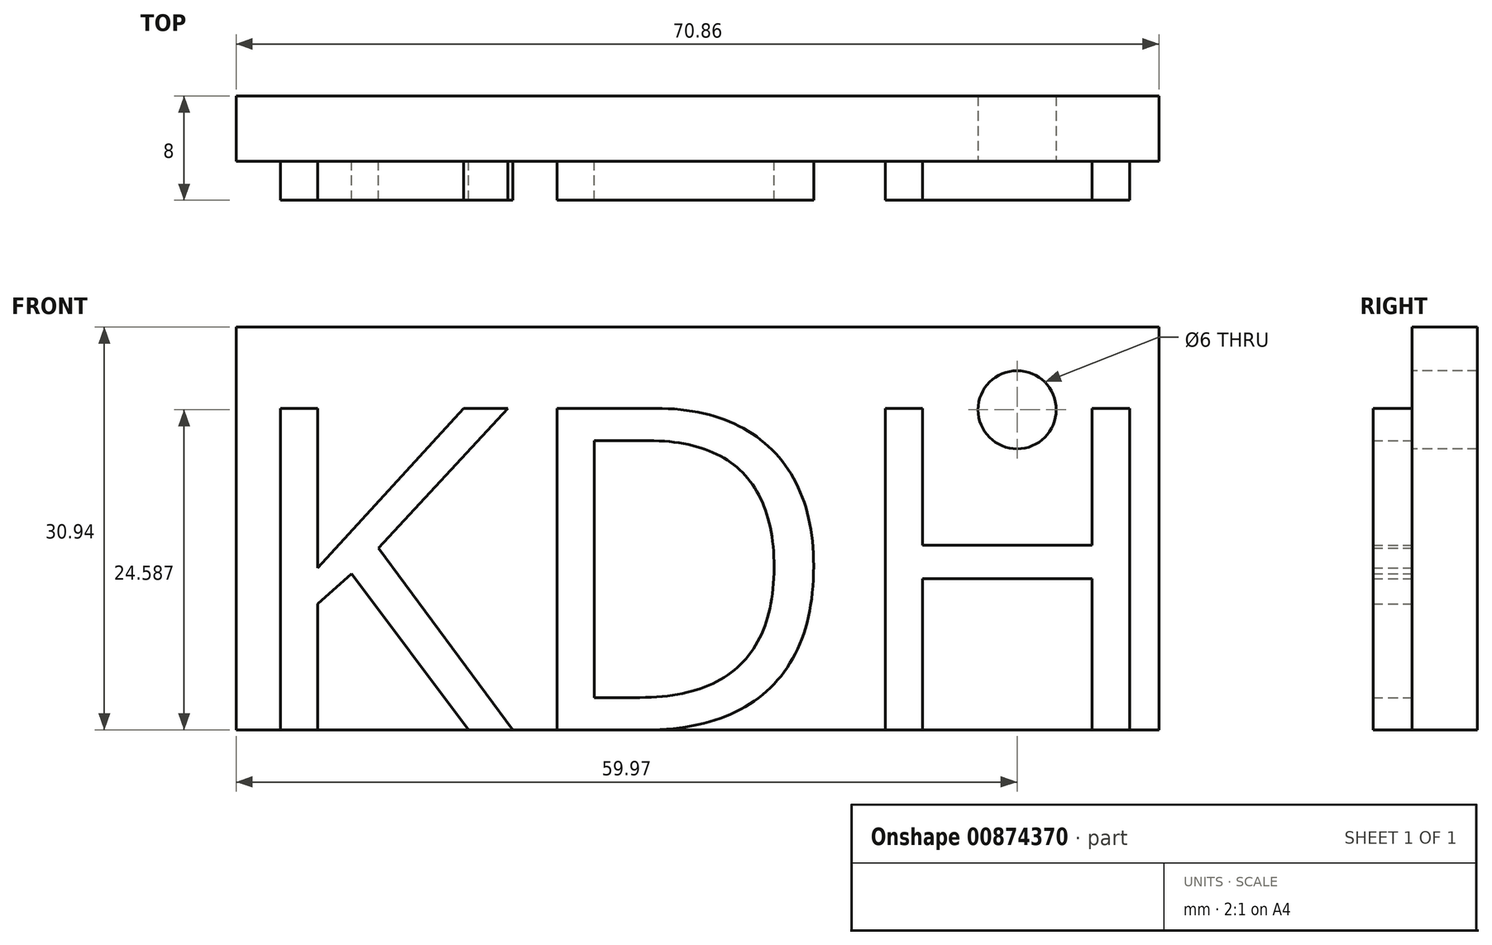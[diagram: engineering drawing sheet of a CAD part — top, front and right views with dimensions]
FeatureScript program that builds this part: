
annotation { "Feature Type Name" : "Feature", "Feature Type Description" : "" }
export const myFeature = defineFeature(function(context is Context, id is Id, definition is map)
    precondition{}
    {
        {
            var Q0;
            Q0=qCreatedBy(makeId("Front.planeOp"),FACE);
            var sketch = newSketch(context, id + "F0", { "sketchPlane" : qUnion([Q0])});
            skLineSegment(sketch, "E0.bottom", {"start": v(0, 0) * mm, "end": v(70.86, 0) * mm});
            skLineSegment(sketch, "E0.top", {"start": v(0, 30.94) * mm, "end": v(70.86, 30.94) * mm});
            skLineSegment(sketch, "E0.left", {"start": v(0, 0) * mm, "end": v(0, 30.94) * mm});
            skLineSegment(sketch, "E0.right", {"start": v(70.86, 0) * mm, "end": v(70.86, 30.94) * mm});
            skSolve(sketch);
        }
        {
            var Q0;
            Q0=makeQuery(id+"F0.imprint","IMPRINT",FACE,{"disambiguationData":[TD([[makeQuery(id+"F0.imprint","IMPRINT",EDGE,{"derivedFrom":sQuery(id+"F0.wireOp",EDGE,"E0.bottom")}),1.0]])]});
            extrude(context, id + "F1", {"entities" : qUnion([Q0]), "depth" : 5 * mm, "offsetDistance" : 25 * mm});
        }
        {
            var Q0;
            Q0=makeQuery(id+"F1.opExtrude","CAP_FACE",FACE,{"disambiguationData":[OSD([sQuery(id+"F0.wireOp",EDGE,"E0.bottom"),sQuery(id+"F0.wireOp",EDGE,"E0.top"),sQuery(id+"F0.wireOp",EDGE,"E0.left"),sQuery(id+"F0.wireOp",EDGE,"E0.right")])],"isStart":false});
            var sketch = newSketch(context, id + "F2", { "sketchPlane" : qUnion([Q0])});
            skText(sketch, "E1", { "text": "KDH", "fontName": "OpenSans-Regular.ttf"});
            const initialGuessF2  = {"E1": [0, 0, 1, 0, 0.02491]};
            skSetInitialGuess(sketch, initialGuessF2);
            skSolve(sketch);
        }
        {
            var Q0;
            Q0 = qSketchRegion(id + "F2", true);
            extrude(context, id + "F3", {"entities" : qUnion([Q0]), "operationType" : NewBodyOperationType.ADD, "depth" : 3 * mm, "offsetDistance" : 25 * mm});
        }
        {
            var Q0;
            {var subQ0=sQuery(id+"F0.wireOp",EDGE,"E0.top");var subQ1=sQuery(id+"F0.wireOp",EDGE,"E0.right");var subQ2=sQuery(id+"F0.wireOp",EDGE,"E0.bottom");var subQ3=sQuery(id+"F0.wireOp",EDGE,"E0.left");Q0=makeQuery(id+"F3.boolean.opBoolean","SPLIT",FACE,{"disambiguationData":[TD([makeQuery(id+"F1.opExtrude","SWEPT_FACE",FACE,{"disambiguationData":[OSD([subQ0])]})])],"derivedFrom":makeQuery(id+"F1.opExtrude","CAP_FACE",FACE,{"disambiguationData":[OSD([subQ2,subQ0,subQ3,subQ1])],"isStart":false})});}
            var sketch = newSketch(context, id + "F4", { "sketchPlane" : qUnion([Q0])});
            skCircle(sketch, "E2", {"center": v(59.97, 24.59) * mm, "radius": 4.89 * mm});
            skSolve(sketch);
        }
        {
            var Q0;
            Q0=sQuery(id+"F4.wireOp",VERTEX,"E2.center");
            var Q1;
            Q1=makeQuery(id+"F1.opExtrude","SWEPT_BODY",BODY,{"disambiguationData":[OSD([sQuery(id+"F0.wireOp",EDGE,"E0.bottom"),sQuery(id+"F0.wireOp",EDGE,"E0.top"),sQuery(id+"F0.wireOp",EDGE,"E0.left"),sQuery(id+"F0.wireOp",EDGE,"E0.right")])]});
            hole(context, id + "F5", {"style" : HoleStyle.SIMPLE, "endStyle" : HoleEndStyle.THROUGH, "holeDiameter" : 6 * mm, "majorDiameter" : 5 * mm, "isTappedThrough" : true, "tappedDepth" : 12 * mm, "tapClearance" : 3, "locations" : qUnion([Q0]), "scope" : qUnion([Q1])});
        }
    });
